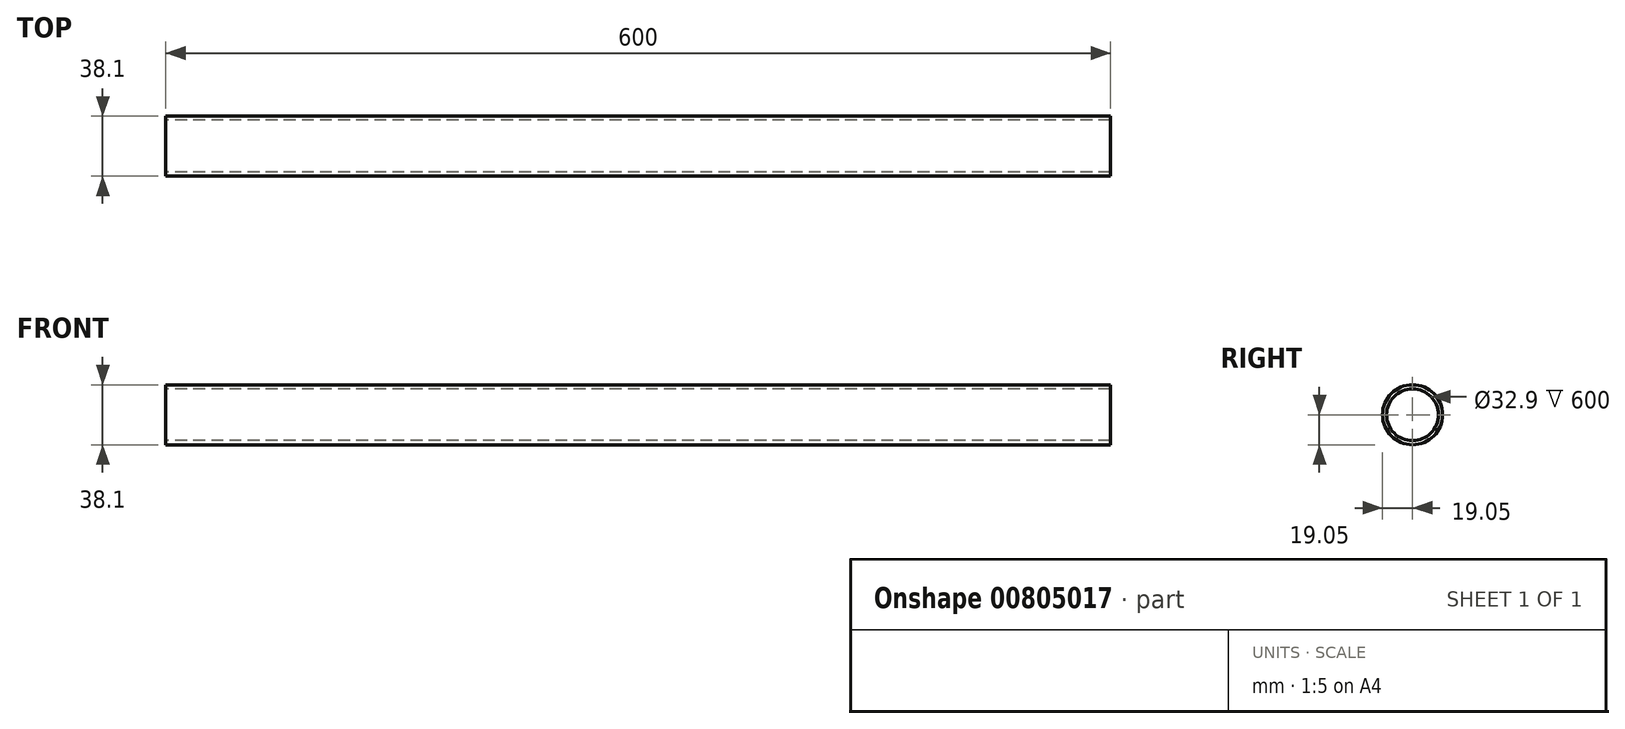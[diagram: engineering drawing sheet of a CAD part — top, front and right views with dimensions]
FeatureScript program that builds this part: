
annotation { "Feature Type Name" : "Feature", "Feature Type Description" : "" }
export const myFeature = defineFeature(function(context is Context, id is Id, definition is map)
    precondition{}
    {
        {
            var Q0;
            Q0=qCreatedBy(makeId("Right.planeOp"),FACE);
            var sketch = newSketch(context, id + "F0", { "sketchPlane" : qUnion([Q0])});
            skCircle(sketch, "E0", {"center": v(0, 0) * mm, "radius": 19.05 * mm});
            skCircle(sketch, "E1", {"center": v(0, 0) * mm, "radius": 16.45 * mm});
            skSolve(sketch);
        }
        {
            var Q0;
            Q0=makeQuery(id+"F0.imprint","IMPRINT",FACE,{"disambiguationData":[TD([[makeQuery(id+"F0.imprint","IMPRINT",EDGE,{"derivedFrom":sQuery(id+"F0.wireOp",EDGE,"E0")}),1.0]])]});
            extrude(context, id + "F1", {"entities" : qUnion([Q0]), "endBound" : BoundingType.SYMMETRIC, "depth" : 600 * mm, "offsetDistance" : 25.4 * mm});
        }
    });
